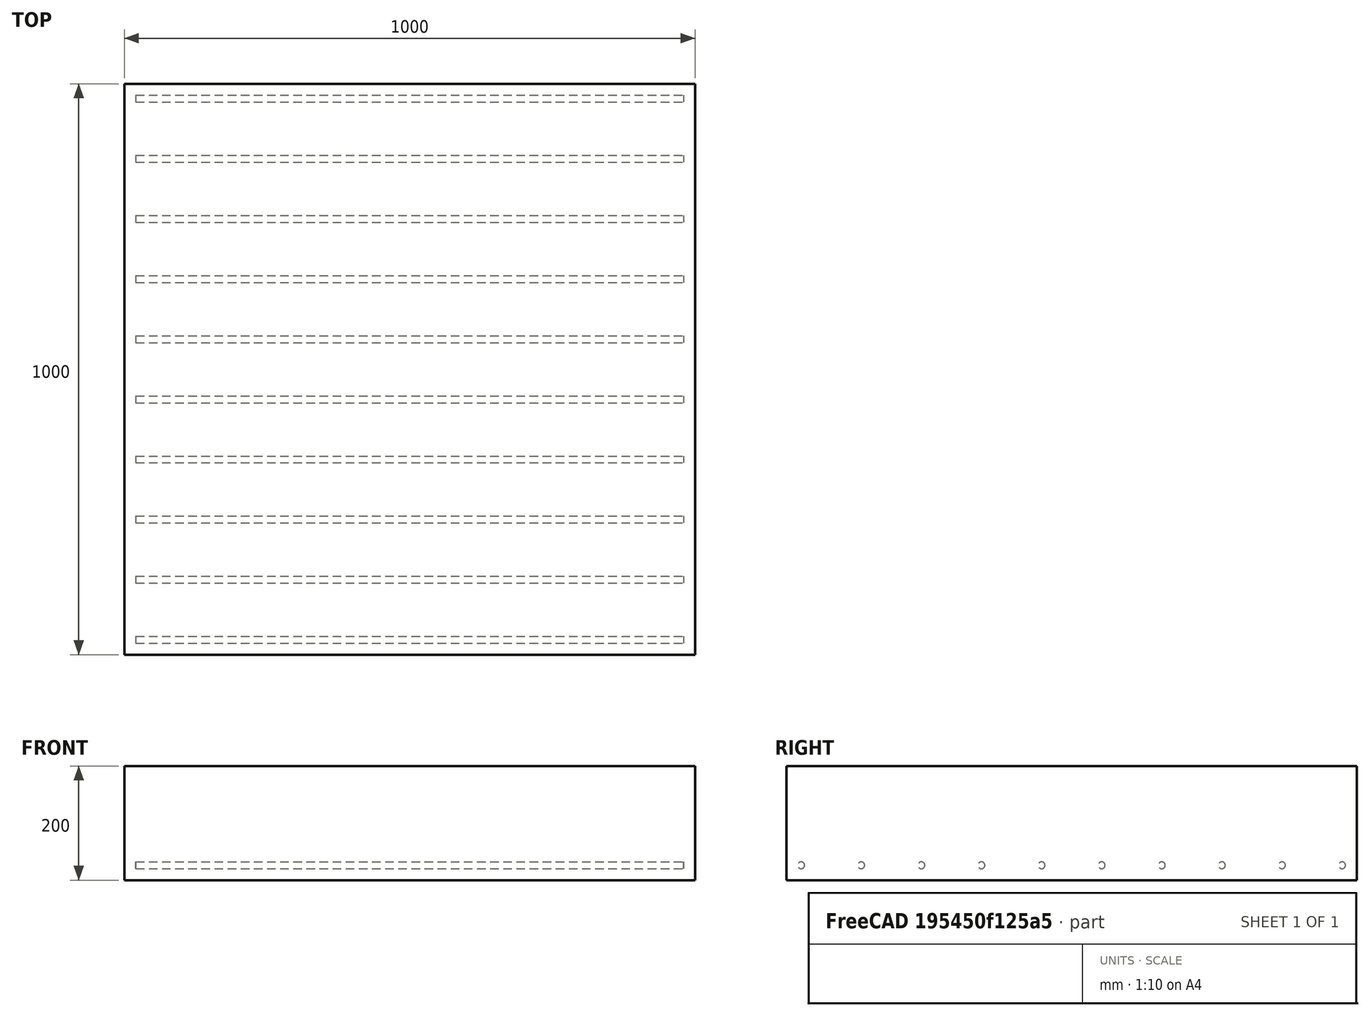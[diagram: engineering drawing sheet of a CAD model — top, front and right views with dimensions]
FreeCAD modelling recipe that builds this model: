
FCSTD DOCUMENT  (FreeCAD 0.21R33771 (Git))
Label: Slab with reinforcement
License: All rights reserved
objects: Part::FeaturePython×2, Part::Part2DObjectPython×1, Sketcher::SketchObject×1
note: 4 computed .brp shape members not serialized (recipe doc carries the construction recipe); baked Part::Feature solids carry a one-line shape summary decoded from their .brp

FEATURE [Part::Part2DObjectPython] Rectangle  # Draft 2D object (typed FeaturePython)
  Area = 1e+06
  ChamferSize = 0
  Columns = 1
  FilletRadius = 0
  Height = 1000
  Length = 1000
  MakeFace = true
  Placement = pos=(4000,-1000,0) rot=(0,0,1;0rad)
  Rows = 1
FEATURE [Part::FeaturePython] Structure  label="Slab"  # Arch/BIM 118 (typed FeaturePython)
  Base = -> Rectangle
  BaseMirror = false
  BaseOffsetX = 0
  BaseOffsetY = 0
  BasePerpendicularToTool = false
  BaseRotation = 0
  ComputedLength = 200
  FaceMaker = 0
  Height = 200
  HorizontalArea = 1e+06
  IfcData = attributes={"GlobalId": {"name": "GlobalId", "type": "IfcGloballyUniqueId", "is_enum": false, "enum_values": []}, "Description": {"... (+453 chars omitted),+1 more (map truncated)
  IfcType = 118
  Length = 1000
  MoveBase = false
  MoveWithHost = false
  Nodes = (4) [(4000,-1000,0),(5000,-1000,0),(5000,0,0),(4000,0,0)]
  NodesOffset = 0
  Normal = (0,0,-1)
  PerimeterLength = 4000
  PredefinedType = 0
  ToolOffsetFirst = 0
  ToolOffsetLast = 0
  VerticalArea = 800000
  Width = 1000
FEATURE [Sketcher::SketchObject] Sketch
  FullyConstrained = false
  MapMode = 5
  Placement = pos=(0,-1000,0) rot=(1,0,0;1.5708rad)
  Support = -> [Structure]
  sketch-geometry (1):
    g0: LineSegment StartX=4020 StartY=-174 StartZ=0 EndX=4980 EndY=-174 EndZ=0
FEATURE [Part::FeaturePython] Rebar  label="StraightRebar"  # Arch/BIM 110 (typed FeaturePython)
  Amount = 10
  AmountCheck = true
  Base = -> Sketch
  Cover = 20
  CoverAlong = Bottom Side
  Diameter = 12
  Direction = (0,0,0)
  Distance = 0
  FrontCover = 20
  HorizontalArea = 0
  Host = -> Structure
  IfcType = 110
  LeftBottomCover = 20
  Length = 960
  Mark = StraightRebar
  MoveBase = false
  MoveWithHost = false
  OffsetEnd = 26
  OffsetStart = 26
  Orientation = Horizontal
  PerimeterLength = 0
  PlacementList = 10 placements: arithmetic series from (0,26,-5.77316e-15) step (0,105.333,-2.33887e-14) to (0,974,-2.16271e-13)
  RebarShape = 0
  RightTopCover = 20
  Rounding = 0
  Spacing = 105.333
  TotalLength = 9600
  TrueSpacing = 10
  VerticalArea = 0
